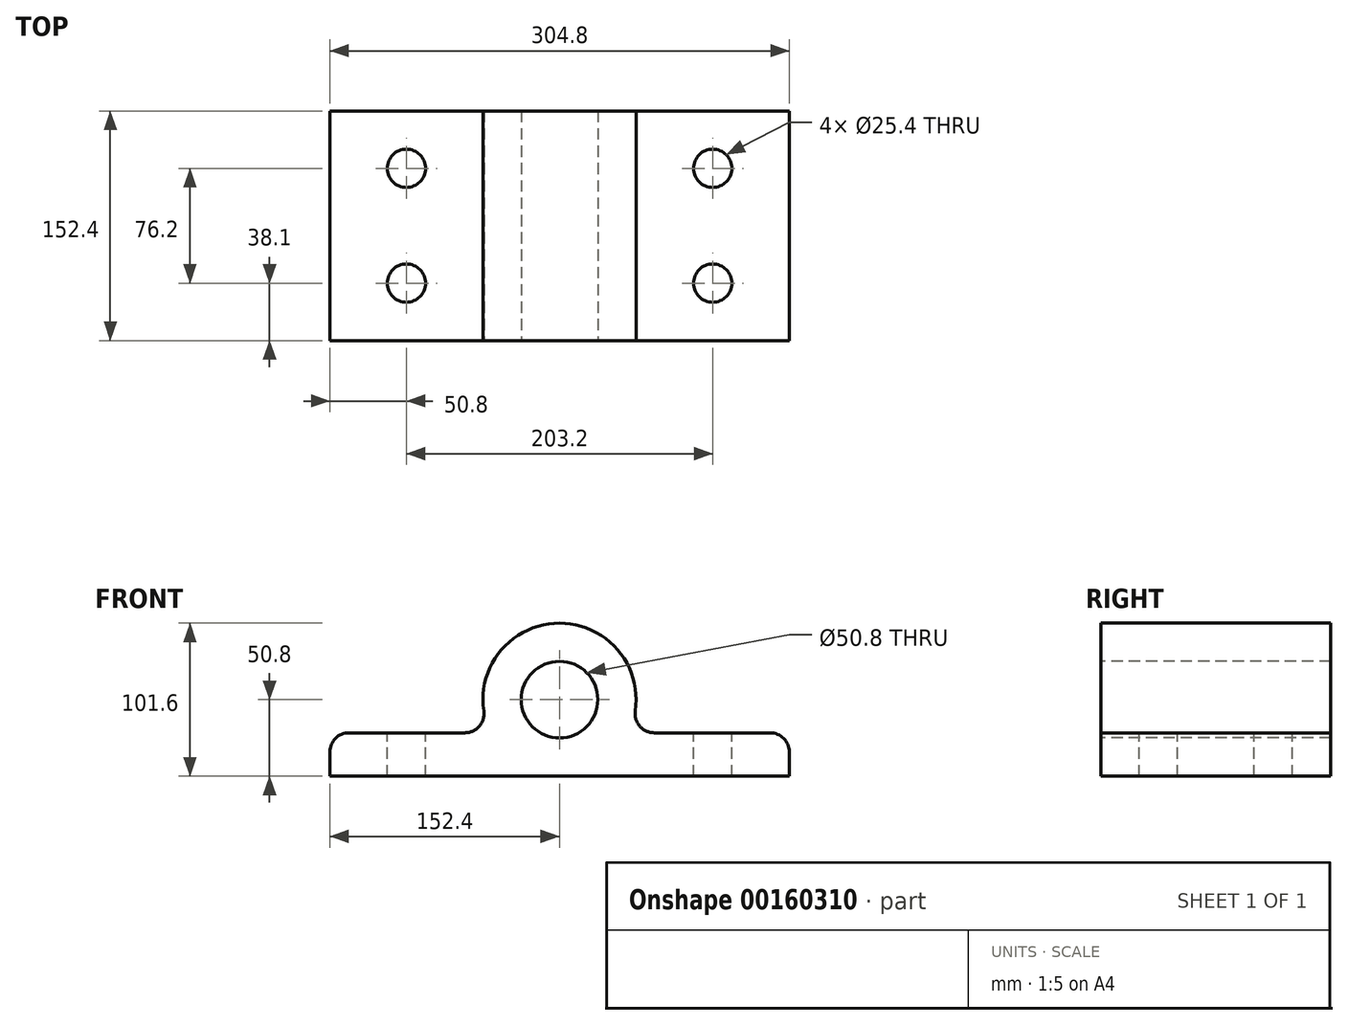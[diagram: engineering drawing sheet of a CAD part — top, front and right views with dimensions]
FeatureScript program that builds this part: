
annotation { "Feature Type Name" : "Feature", "Feature Type Description" : "" }
export const myFeature = defineFeature(function(context is Context, id is Id, definition is map)
    precondition{}
    {
        {
            var Q0;
            Q0=qCreatedBy(makeId("Front.planeOp"),FACE);
            var sketch = newSketch(context, id + "F0", { "sketchPlane" : qUnion([Q0])});
            skArc(sketch, "E0", {"start": v(50.25, -7.47) * mm, "mid": v(0, 50.8) * mm, "end": v(-50.25, -7.47) * mm});
            skCircle(sketch, "E1", {"center": v(0, 0) * mm, "radius": 25.4 * mm});
            skLineSegment(sketch, "E2", {"start": v(62.8, -22.04) * mm, "end": v(139.7, -22.04) * mm});
            skLineSegment(sketch, "E3", {"start": v(152.4, -34.74) * mm, "end": v(152.4, -50.8) * mm});
            skLineSegment(sketch, "E4", {"start": v(152.4, -50.8) * mm, "end": v(-152.4, -50.8) * mm});
            skLineSegment(sketch, "E5", {"start": v(-152.4, -50.8) * mm, "end": v(-152.4, -34.74) * mm});
            skLineSegment(sketch, "E6", {"start": v(-139.7, -22.04) * mm, "end": v(-62.8, -22.04) * mm});
            skPoint(sketch, "E7.visualSharp", {"position": v(152.4, -22.04) * mm});
            skArc(sketch, "E7.filletArc", {"start": v(152.4, -34.74) * mm, "mid": v(148.68, -25.76) * mm, "end": v(139.7, -22.04) * mm});
            skPoint(sketch, "E8.visualSharp", {"position": v(-152.4, -22.04) * mm});
            skArc(sketch, "E8.filletArc", {"start": v(-139.7, -22.04) * mm, "mid": v(-148.68, -25.76) * mm, "end": v(-152.4, -34.74) * mm});
            skPoint(sketch, "E9.visualSharp", {"position": v(-45.77, -22.04) * mm});
            skArc(sketch, "E9.filletArc", {"start": v(-62.8, -22.04) * mm, "mid": v(-53.2, -17.63) * mm, "end": v(-50.25, -7.47) * mm});
            skPoint(sketch, "E10.visualSharp", {"position": v(45.77, -22.04) * mm});
            skArc(sketch, "E10.filletArc", {"start": v(50.25, -7.47) * mm, "mid": v(53.2, -17.63) * mm, "end": v(62.8, -22.04) * mm});
            skSolve(sketch);
        }
        {
            var Q0;
            Q0=makeQuery(id+"F0.imprint","IMPRINT",FACE,{"disambiguationData":[TD([[makeQuery(id+"F0.imprint","IMPRINT",EDGE,{"derivedFrom":sQuery(id+"F0.wireOp",EDGE,"E0")}),1.0]])]});
            extrude(context, id + "F1", {"entities" : qUnion([Q0]), "oppositeDirection" : true, "depth" : 152.4 * mm});
        }
        {
            var Q0;
            Q0=makeQuery(id+"F1.opExtrude","SWEPT_FACE",FACE,{"disambiguationData":[OSD([sQuery(id+"F0.wireOp",EDGE,"E6")])]});
            cPlane(context, id + "F2", {"entities" : qUnion([Q0]), "cplaneType" : CPlaneType.OFFSET, "offset" : 0 * mm, "width" : 152.4 * mm, "height" : 152.4 * mm});
        }
        {
            var Q0;
            Q0=qCreatedBy(id+"F2.planeOp",FACE);
            var sketch = newSketch(context, id + "F3", { "sketchPlane" : qUnion([Q0])});
            skCircle(sketch, "E11", {"center": v(101.6, 114.3) * mm, "radius": 12.7 * mm});
            skCircle(sketch, "E12", {"center": v(101.6, 38.1) * mm, "radius": 12.7 * mm});
            skCircle(sketch, "E13", {"center": v(-101.6, 114.3) * mm, "radius": 12.7 * mm});
            skCircle(sketch, "E14", {"center": v(-101.6, 38.1) * mm, "radius": 12.7 * mm});
            skSolve(sketch);
        }
        {
            var Q0;
            Q0 = qSketchRegion(id + "F3", true);
            extrude(context, id + "F4", {"entities" : qUnion([Q0]), "operationType" : NewBodyOperationType.REMOVE, "oppositeDirection" : true, "depth" : 76.2 * mm});
        }
    });
